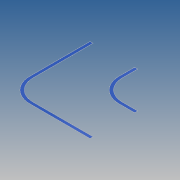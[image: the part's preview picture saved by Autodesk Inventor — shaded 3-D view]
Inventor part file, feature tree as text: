
AUTODESK INVENTOR PART (.ipt)
format: ipt  version: 2020 (Build 240168000, 168)  size: 107,008 bytes
history: native  units: mm
features: extrude x1, sketch x1
ambient origin geometry x8: Origin, YZ Plane, XZ Plane, XY Plane, X Axis, Y Axis, Z Axis, Center Point
bodies: Solid1 (feature_tree)
feature tree (2):
  extrude  "Extrusion1"  Depth=30.0mm
  sketch  "Sketch1"  dims[d3=430.0mm d25=30.0mm d26=150.0mm d27=400.0mm d28=400.0mm d29=0.5mm d30=0.0mm]
